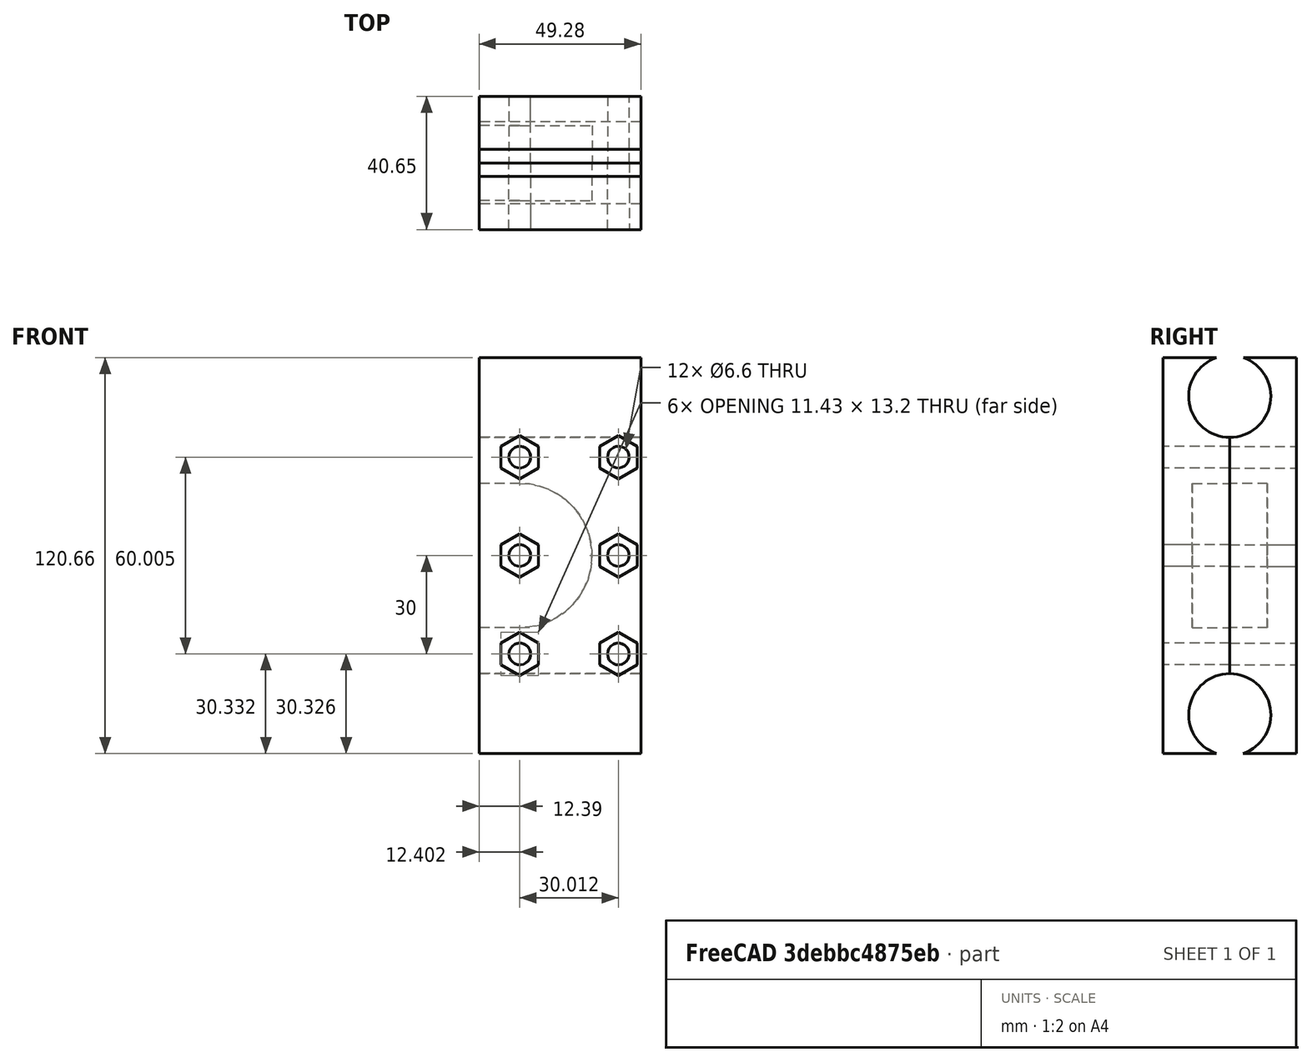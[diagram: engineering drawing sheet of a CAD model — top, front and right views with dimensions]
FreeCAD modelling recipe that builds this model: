
FCSTD DOCUMENT  (FreeCAD 0.16R6712 (Git))
Label: idler assembly
License: All rights reserved
LicenseURL: http://en.wikipedia.org/wiki/All_rights_reserved
objects: Part::Feature×2, PartDesign::Pocket×2
note: 6 computed .brp shape members not serialized (recipe doc carries the construction recipe); baked Part::Feature solids carry a one-line shape summary decoded from their .brp

FEATURE [Part::Feature] Pocket  label="Idler Half 2 Y Axis"
  Placement = pos=(28.9416,-63.0289,-60.3284) rot=(0,-0.707107,0.707107;3.14159rad)
  shape: bbox 49.27 x 20.32 x 120.6 mm, 60 faces (baked)
FEATURE [Part::Feature] Pocket005  label="Idler Half 1 Y Axis001"
  Placement = pos=(28.9295,-63.0207,-60.3338) rot=(0,0.707107,0.707107;3.14159rad)
  shape: bbox 49.27 x 20.32 x 120.6 mm, 60 faces (baked)
FEATURE [PartDesign::Pocket] Pocket007  label="Bearing"
  Length = 0.2
  Placement = pos=(28.9108,-55.9687,-60.4137) rot=(1,0,0;1.5708rad)
  Type = 0
FEATURE [PartDesign::Pocket] Pocket008  label="Bearing001"
  Length = 0.2
  Placement = pos=(28.9108,-55.9687,-60.4137) rot=(1,0,0;1.5708rad)
  Type = 0
